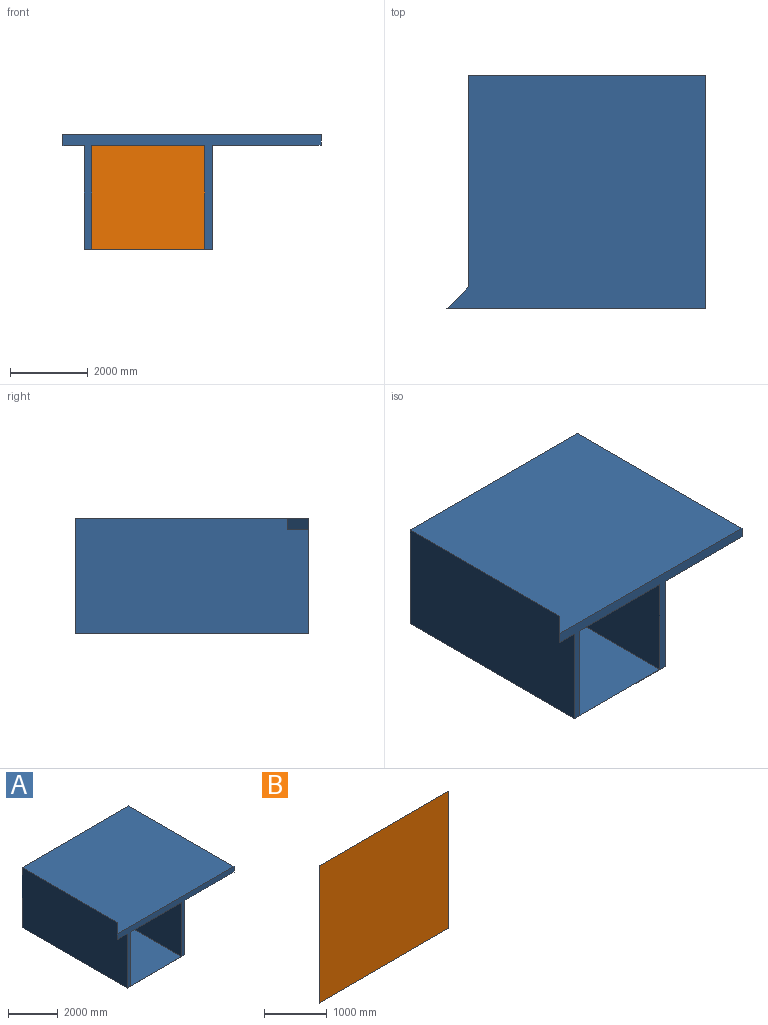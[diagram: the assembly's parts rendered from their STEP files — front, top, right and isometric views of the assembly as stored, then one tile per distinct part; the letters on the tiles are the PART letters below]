
ASSEMBLY  parts=2 mates=1
PART A: 15 faces, bbox 6650x6001x2955.1 mm
  f0: plane 6001x2955.1mm, normal (-1,0,0), area 17573851mm2, adj f5,f6,f7,f8,f9,f10,f13,f14
  f1: plane 6001x2685.1mm, normal (1,0,0), area 16110600.4mm2, adj f6,f7,f8,f9,f10,f11
  f2: plane 6000x2670mm, normal (1,0,0), area 16020000mm2, adj f3,f6,f7,f8
  f3: plane 6000x2920mm, normal (0,0,-1), area 17520000mm2, adj f2,f4,f6,f7
  f4: plane 6000x2670mm, normal (-1,0,0), area 16020000mm2, adj f3,f6,f7,f8
  f5: plane 6650x6000mm, normal (0,0,1), area 36751250mm2, adj f0,f6,f7,f12,f13
  f6: plane 6650x2955.1mm, normal (0,-1,0), area 2868180.8mm2, adj f0,f1,f2,f3,f4,f5,f8,f10
  f7: plane 6100x2955mm, normal (0,1,0), area 2711100.3mm2, adj f0,f1,f2,f3,f4,f5,f8,f11
  f8: plane 6001x3300mm, normal (0,0,1), area 17523300mm2, adj f0,f1,f2,f4,f6,f7,f9
  f9: plane 3300x0.1mm, normal (0,1,0), area 330.5mm2, adj f0,f1,f8,f10
  f10: plane 6001x3300mm, normal (0,0,-1), area 19803300mm2, adj f0,f1,f6,f9
  f11: plane 6000x2800mm, normal (0,0,-1), area 16800000mm2, adj f1,f6,f7,f12
  f12: plane 6000x270mm, normal (1,0,0), area 1620000.6mm2, adj f5,f6,f7,f11
  f13: plane 550x550mm, normal (-0.71,0.71,0), area 221678mm2, adj f0,f5,f6,f14
  f14: plane 550x550mm, normal (0,0,-1), area 151250mm2, adj f0,f6,f13
PART B: 6 faces, bbox 2920x0x2670 mm
  f0: plane 2670x0.03mm, normal (-1,0,0), area 80.1mm2, adj f1,f3,f4,f5
  f1: plane 2920x0.03mm, normal (0,0,-1), area 87.6mm2, adj f0,f2,f4,f5
  f2: plane 2670x0.03mm, normal (1,0,0), area 80.1mm2, adj f1,f3,f4,f5
  f3: plane 2920x0.03mm, normal (0,0,1), area 87.6mm2, adj f0,f2,f4,f5
  f4: plane 2920x2670mm, normal (0,-1,0), area 7796400mm2, adj f0,f1,f2,f3
  f5: plane 2920x2670mm, normal (0,1,0), area 7796400mm2, adj f0,f1,f2,f3
PLACE A t=(30.68,1988.2,-78.18)mm
PLACE B t=(30.68,1988.22,-78.18)mm
MATE planar B.f5 <-> A.f7  axis (0,1,0) through (1490.68,1988.2,2591.82)mm
